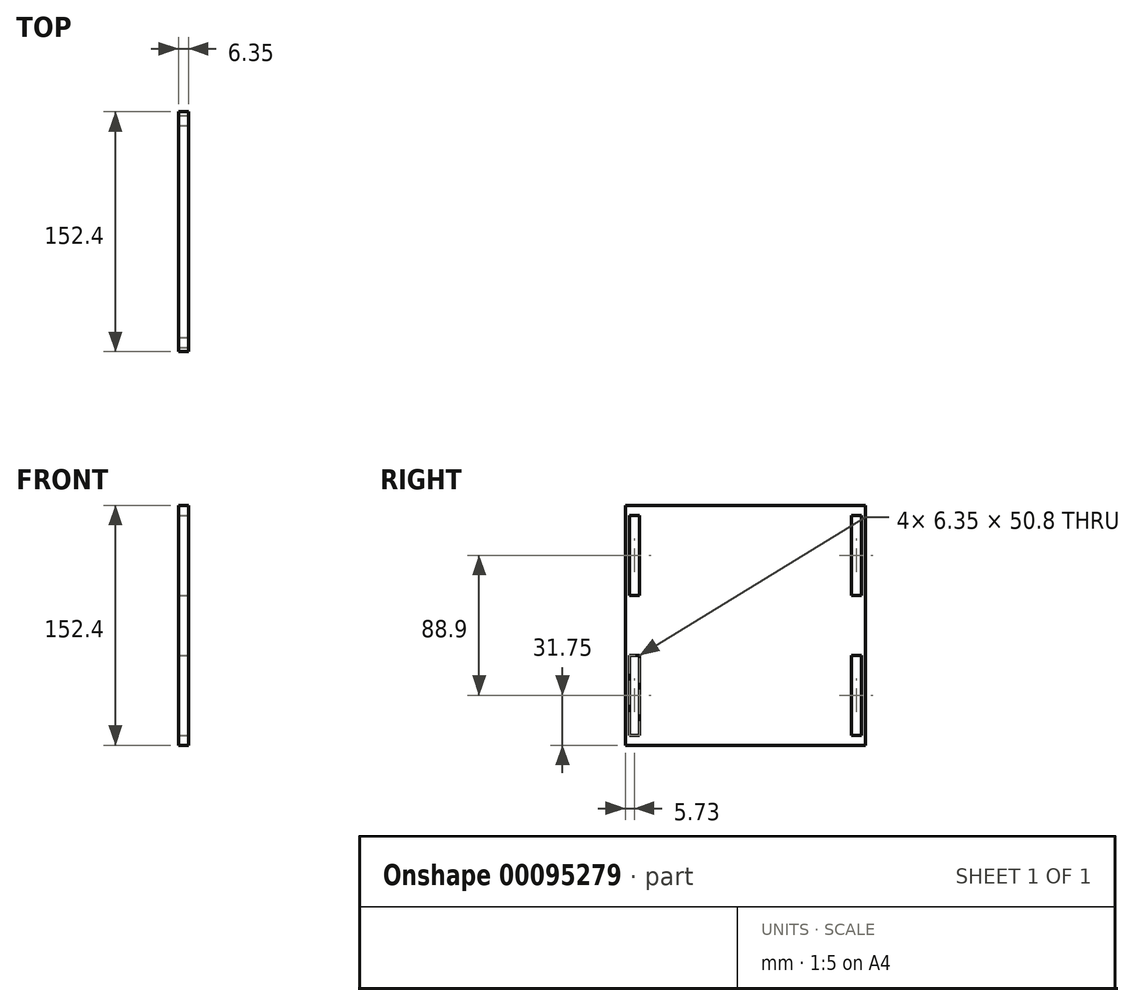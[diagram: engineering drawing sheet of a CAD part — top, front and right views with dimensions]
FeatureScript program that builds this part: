
annotation { "Feature Type Name" : "Feature", "Feature Type Description" : "" }
export const myFeature = defineFeature(function(context is Context, id is Id, definition is map)
    precondition{}
    {
        {
            var Q0;
            Q0=qCreatedBy(makeId("Right.planeOp"),FACE);
            var sketch = newSketch(context, id + "F0", { "sketchPlane" : qUnion([Q0])});
            skLineSegment(sketch, "E0.bottom", {"start": v(76.2, -76.2) * mm, "end": v(-76.2, -76.2) * mm});
            skLineSegment(sketch, "E0.top", {"start": v(76.2, 76.2) * mm, "end": v(-76.2, 76.2) * mm});
            skLineSegment(sketch, "E0.left", {"start": v(76.2, -76.2) * mm, "end": v(76.2, 76.2) * mm});
            skLineSegment(sketch, "E0.right", {"start": v(-76.2, -76.2) * mm, "end": v(-76.2, 76.2) * mm});
            skPoint(sketch, "E0.middle", {"position": v(0, 0) * mm});
            skSolve(sketch);
        }
        {
            var Q0;
            Q0 = qSketchRegion(id + "F0", true);
            extrude(context, id + "F1", {"entities" : qUnion([Q0]), "depth" : 6.35 * mm});
        }
        {
            var Q0;
            Q0=makeQuery(id+"F1.opExtrude","CAP_FACE",FACE,{"disambiguationData":[OSD([sQuery(id+"F0.wireOp",EDGE,"E0.bottom"),sQuery(id+"F0.wireOp",EDGE,"E0.top"),sQuery(id+"F0.wireOp",EDGE,"E0.left"),sQuery(id+"F0.wireOp",EDGE,"E0.right")])],"isStart":false});
            var sketch = newSketch(context, id + "F2", { "sketchPlane" : qUnion([Q0])});
            skLineSegment(sketch, "E1.bottom", {"start": v(67.3, 69.85) * mm, "end": v(73.64, 69.85) * mm});
            skLineSegment(sketch, "E1.top", {"start": v(67.3, 19.05) * mm, "end": v(73.64, 19.05) * mm});
            skLineSegment(sketch, "E1.left", {"start": v(67.3, 69.85) * mm, "end": v(67.3, 19.05) * mm});
            skLineSegment(sketch, "E1.right", {"start": v(73.64, 69.85) * mm, "end": v(73.64, 19.05) * mm});
            skLineSegment(sketch, "E2.MirrorCS", {"start": v(67.3, -19.05) * mm, "end": v(73.64, -19.05) * mm});
            skLineSegment(sketch, "E3.MirrorCS", {"start": v(67.3, -69.85) * mm, "end": v(67.3, -19.05) * mm});
            skLineSegment(sketch, "E4.MirrorCS", {"start": v(73.64, -69.85) * mm, "end": v(73.64, -19.05) * mm});
            skLineSegment(sketch, "E5.MirrorCS", {"start": v(67.3, -69.85) * mm, "end": v(73.64, -69.85) * mm});
            skLineSegment(sketch, "E6.MirrorCS", {"start": v(-67.3, 69.85) * mm, "end": v(-67.3, 19.05) * mm});
            skLineSegment(sketch, "E7.MirrorCS", {"start": v(-67.3, 69.85) * mm, "end": v(-73.64, 69.85) * mm});
            skLineSegment(sketch, "E8.MirrorCS", {"start": v(-73.64, 69.85) * mm, "end": v(-73.64, 19.05) * mm});
            skLineSegment(sketch, "E9.MirrorCS", {"start": v(-67.3, 19.05) * mm, "end": v(-73.64, 19.05) * mm});
            skLineSegment(sketch, "E10.MirrorCS", {"start": v(-67.3, -19.05) * mm, "end": v(-73.64, -19.05) * mm});
            skLineSegment(sketch, "E11.MirrorCS", {"start": v(-67.3, -69.85) * mm, "end": v(-67.3, -19.05) * mm});
            skLineSegment(sketch, "E12.MirrorCS", {"start": v(-73.64, -69.85) * mm, "end": v(-73.64, -19.05) * mm});
            skLineSegment(sketch, "E13.MirrorCS", {"start": v(-67.3, -69.85) * mm, "end": v(-73.64, -69.85) * mm});
            skSolve(sketch);
        }
        {
            var Q0;
            Q0=makeQuery(id+"F2.imprint","IMPRINT",FACE,{"disambiguationData":[TD([[makeQuery(id+"F2.imprint","IMPRINT",EDGE,{"derivedFrom":sQuery(id+"F2.wireOp",EDGE,"E6.MirrorCS")}),-1.0]])]});
            var Q1;
            Q1=makeQuery(id+"F2.imprint","IMPRINT",FACE,{"disambiguationData":[TD([[makeQuery(id+"F2.imprint","IMPRINT",EDGE,{"derivedFrom":sQuery(id+"F2.wireOp",EDGE,"E1.bottom")}),-1.0]])]});
            var Q2;
            Q2=makeQuery(id+"F2.imprint","IMPRINT",FACE,{"disambiguationData":[TD([[makeQuery(id+"F2.imprint","IMPRINT",EDGE,{"derivedFrom":sQuery(id+"F2.wireOp",EDGE,"E2.MirrorCS")}),-1.0]])]});
            var Q3;
            Q3=makeQuery(id+"F2.imprint","IMPRINT",FACE,{"disambiguationData":[TD([[makeQuery(id+"F2.imprint","IMPRINT",EDGE,{"derivedFrom":sQuery(id+"F2.wireOp",EDGE,"E10.MirrorCS")}),1.0]])]});
            extrude(context, id + "F3", {"entities" : qUnion([Q0, Q1, Q2, Q3]), "operationType" : NewBodyOperationType.REMOVE, "oppositeDirection" : true, "depth" : 25.4 * mm});
        }
    });
